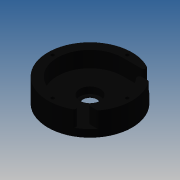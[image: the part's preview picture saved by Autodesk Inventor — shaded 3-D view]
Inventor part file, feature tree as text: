
AUTODESK INVENTOR PART (.ipt)
format: ipt  version: 2013 (Build 170138000, 138)  size: 188,416 bytes
history: native  units: mm
features: extrude x10, sketch x10, fillet x2, pattern_circular x1
ambient origin geometry x8: Origin, YZ Plane, XZ Plane, XY Plane, X Axis, Y Axis, Z Axis, Center Point
bodies: Solid1 (feature_tree)
feature tree (23):
  extrude  "Extrusion1"  Depth=70.0mm
  extrude  "Extrusion2"  Depth=8.0mm TaperAngle=0.0deg
  extrude  "Extrusion3"  Depth=10.0mm TaperAngle=0.0deg
  extrude  "Extrusion4"  Depth=7.0mm TaperAngle=0.0deg
  extrude  "Extrusion5"  Depth=7.5mm
  fillet  "Fillet1"  Radius=7.0mm
  extrude  "Extrusion6"  Depth=40.0mm
  extrude  "Extrusion7"  Depth=7.0mm TaperAngle=0.0deg
  pattern_circular  "Circular Pattern1"  Count=4 Angle=360.0deg
  extrude  "Extrusion8"  Depth=3.5mm
  extrude  "Extrusion9"  Depth=3.0mm TaperAngle=0.0deg
  extrude  "Extrusion10"  Depth=5.5mm
  fillet  "Fillet2"  Radius=4.0mm
  sketch  "Sketch1"  dims[d0=90.0mm d2=70.0mm]
  sketch  "Sketch2"  dims[d3=25.0mm d4=0.0mm d5=8.0mm d6=0.0mm]
  sketch  "Sketch3"  dims[d7=15.0mm d9=10.0mm d10=0.0mm]
  sketch  "Sketch4"  dims[d11=22.0mm d13=7.0mm d14=0.0mm]
  sketch  "Sketch5"  dims[d15=65.0mm d17=7.5mm d18=7.0mm d19=0.0mm]
  sketch  "Sketch6"  dims[d20=2.5mm d21=40.0mm]
  sketch  "Sketch7"  dims[d22=3.5mm d23=7.0mm d24=0.0mm]
  sketch  "Sketch8"  dims[d25=6.0mm]
  sketch  "Sketch9"  dims[d27=3.0mm d28=0.0mm d29=40.0mm d30=360.0deg]
  sketch  "Sketch10"  dims[d32=20.0mm d34=3.5mm d35=3.0mm d36=0.0mm d37=5.5mm d38=4.0mm d39=0.0mm d40=10.0mm d41=0.0mm d42=3.5mm]
